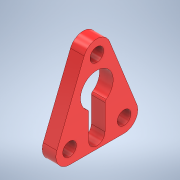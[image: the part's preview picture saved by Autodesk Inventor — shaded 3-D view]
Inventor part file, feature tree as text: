
AUTODESK INVENTOR PART (.ipt)
format: ipt  version: 2021 (Build 250183000, 183)  size: 146,944 bytes
history: native  units: mm
features: extrude x2, sketch x2
ambient origin geometry x8: Origin, YZ Plane, XZ Plane, XY Plane, X Axis, Y Axis, Z Axis, Center Point
bodies: Solid1 (feature_tree)
feature tree (4):
  extrude  "Extrusion1"  Depth=10.0mm TaperAngle=0.0deg
  extrude  "Extrusion2"  Depth=30.0mm
  sketch  "Sketch1"  dims[d9=6.0mm d10=3.0mm d13=10.0mm d14=0.0mm]
  sketch  "Sketch2"  dims[d15=24.0mm d16=30.0mm d17=12.0mm d18=2.0mm d19=28.0mm d20=20.0mm d21=40.0mm d22=10.0mm d23=10.0mm d24=22.0mm d25=10.0mm d26=20.0mm d27=20.0mm d28=20.0mm d29=10.0mm d30=0.0mm]
